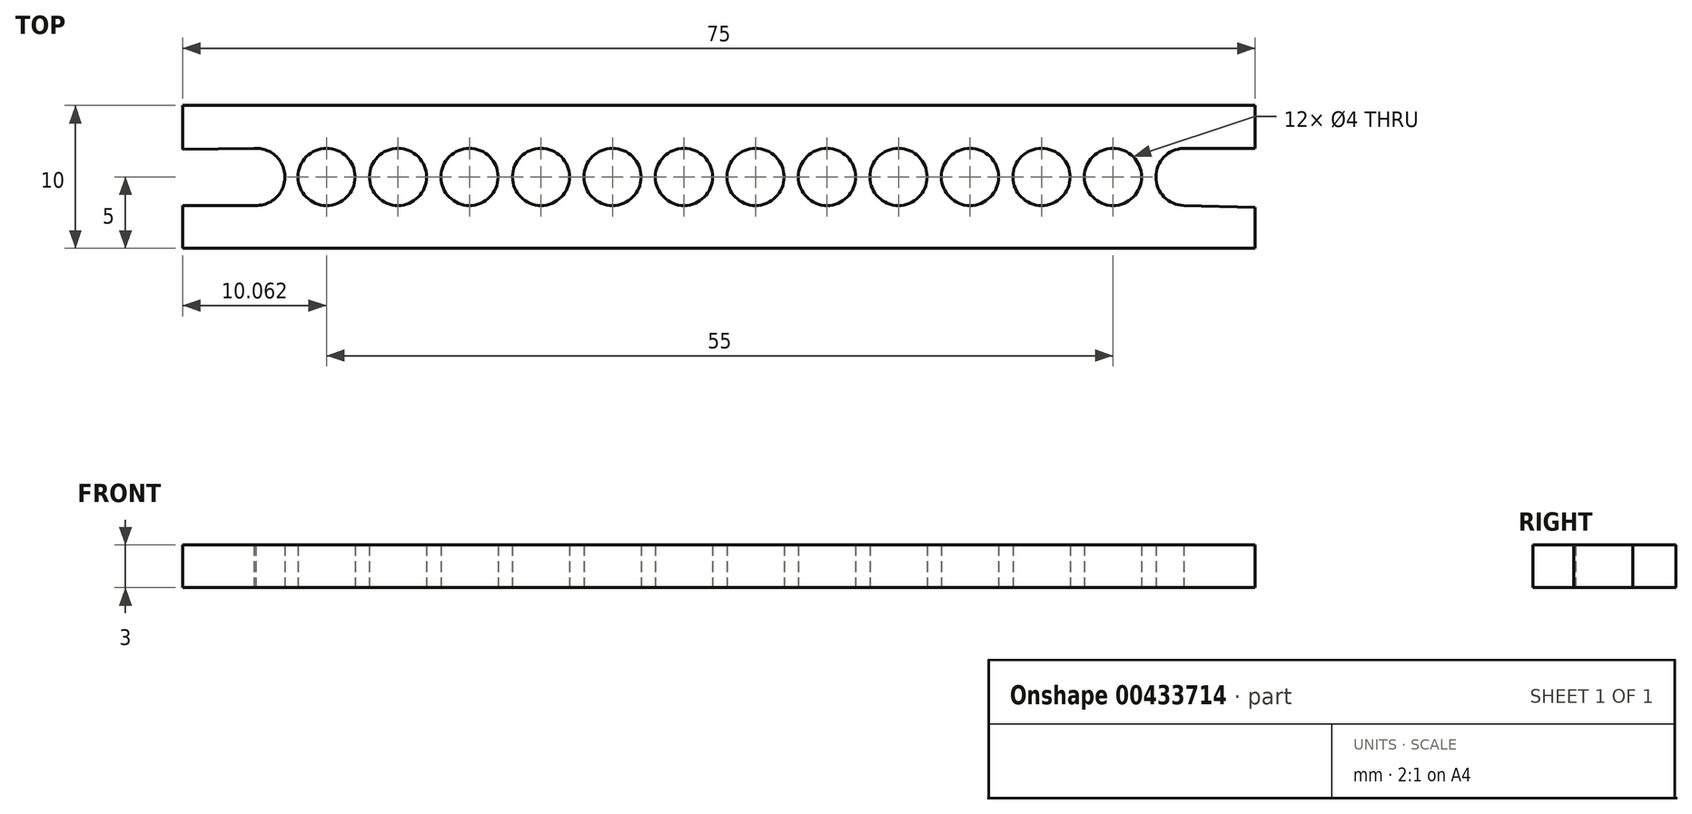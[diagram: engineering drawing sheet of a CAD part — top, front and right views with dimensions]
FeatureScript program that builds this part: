
annotation { "Feature Type Name" : "Feature", "Feature Type Description" : "" }
export const myFeature = defineFeature(function(context is Context, id is Id, definition is map)
    precondition{}
    {
        {
            var Q0;
            Q0=qCreatedBy(makeId("Top.planeOp"),FACE);
            var sketch = newSketch(context, id + "F0", { "sketchPlane" : qUnion([Q0])});
            skLineSegment(sketch, "E0.bottom", {"start": v(37.5, -5) * mm, "end": v(-37.5, -5) * mm});
            skLineSegment(sketch, "E0.top", {"start": v(37.5, 5) * mm, "end": v(-37.5, 5) * mm});
            skLineSegment(sketch, "E0.left", {"start": v(37.5, -5) * mm, "end": v(37.5, -2.13) * mm});
            skLineSegment(sketch, "E0.right", {"start": v(-37.5, -5) * mm, "end": v(-37.5, -2) * mm});
            skPoint(sketch, "E0.middle", {"position": v(0, 0) * mm});
            skCircle(sketch, "E1", {"center": v(-22.44, 0) * mm, "radius": 2 * mm});
            skCircle(sketch, "E2", {"center": v(-17.44, 0) * mm, "radius": 2 * mm});
            skCircle(sketch, "E3", {"center": v(-12.44, 0) * mm, "radius": 2 * mm});
            skCircle(sketch, "E4", {"center": v(-7.44, 0) * mm, "radius": 2 * mm});
            skCircle(sketch, "E5", {"center": v(-2.44, 0) * mm, "radius": 2 * mm});
            skCircle(sketch, "E6", {"center": v(2.56, 0) * mm, "radius": 2 * mm});
            skCircle(sketch, "E7", {"center": v(7.56, 0) * mm, "radius": 2 * mm});
            skCircle(sketch, "E8", {"center": v(12.56, 0) * mm, "radius": 2 * mm});
            skCircle(sketch, "E9", {"center": v(17.56, 0) * mm, "radius": 2 * mm});
            skCircle(sketch, "E10", {"center": v(22.56, 0) * mm, "radius": 2 * mm});
            skCircle(sketch, "E11", {"center": v(27.56, 0) * mm, "radius": 2 * mm});
            skCircle(sketch, "E12", {"center": v(-27.44, 0) * mm, "radius": 2 * mm});
            skArc(sketch, "E13", {"start": v(32.62, 2) * mm, "mid": v(30.56, 0.06) * mm, "end": v(32.5, -2) * mm});
            skArc(sketch, "E14", {"start": v(-32.39, -2) * mm, "mid": v(-30.35, 0.07) * mm, "end": v(-32.52, 2) * mm});
            skLineSegment(sketch, "E15", {"start": v(-32.52, 2) * mm, "end": v(-37.52, 1.94) * mm});
            skLineSegment(sketch, "E16", {"start": v(-32.39, -2) * mm, "end": v(-37.5, -2) * mm});
            skLineSegment(sketch, "E17", {"start": v(32.5, 2) * mm, "end": v(37.5, 2) * mm});
            skLineSegment(sketch, "E18", {"start": v(32.5, -2) * mm, "end": v(37.5, -2.13) * mm});
            skLineSegment(sketch, "E19.trimOffspring", {"start": v(37.5, 2) * mm, "end": v(37.5, 5) * mm});
            skLineSegment(sketch, "E20.trimOffspring", {"start": v(-37.5, 1.94) * mm, "end": v(-37.5, 5) * mm});
            skPoint(sketch, "E21.startSnap0", {"position": v(-30.35, 0.07) * mm});
            skLineSegment(sketch, "E22", {"start": v(-5.44, 0) * mm, "end": v(-4.44, 0) * mm});
            skSolve(sketch);
        }
        {
            var Q0;
            Q0 = qSketchRegion(id + "F0", true);
            extrude(context, id + "F1", {"entities" : qUnion([Q0]), "depth" : 3 * mm});
        }
    });
